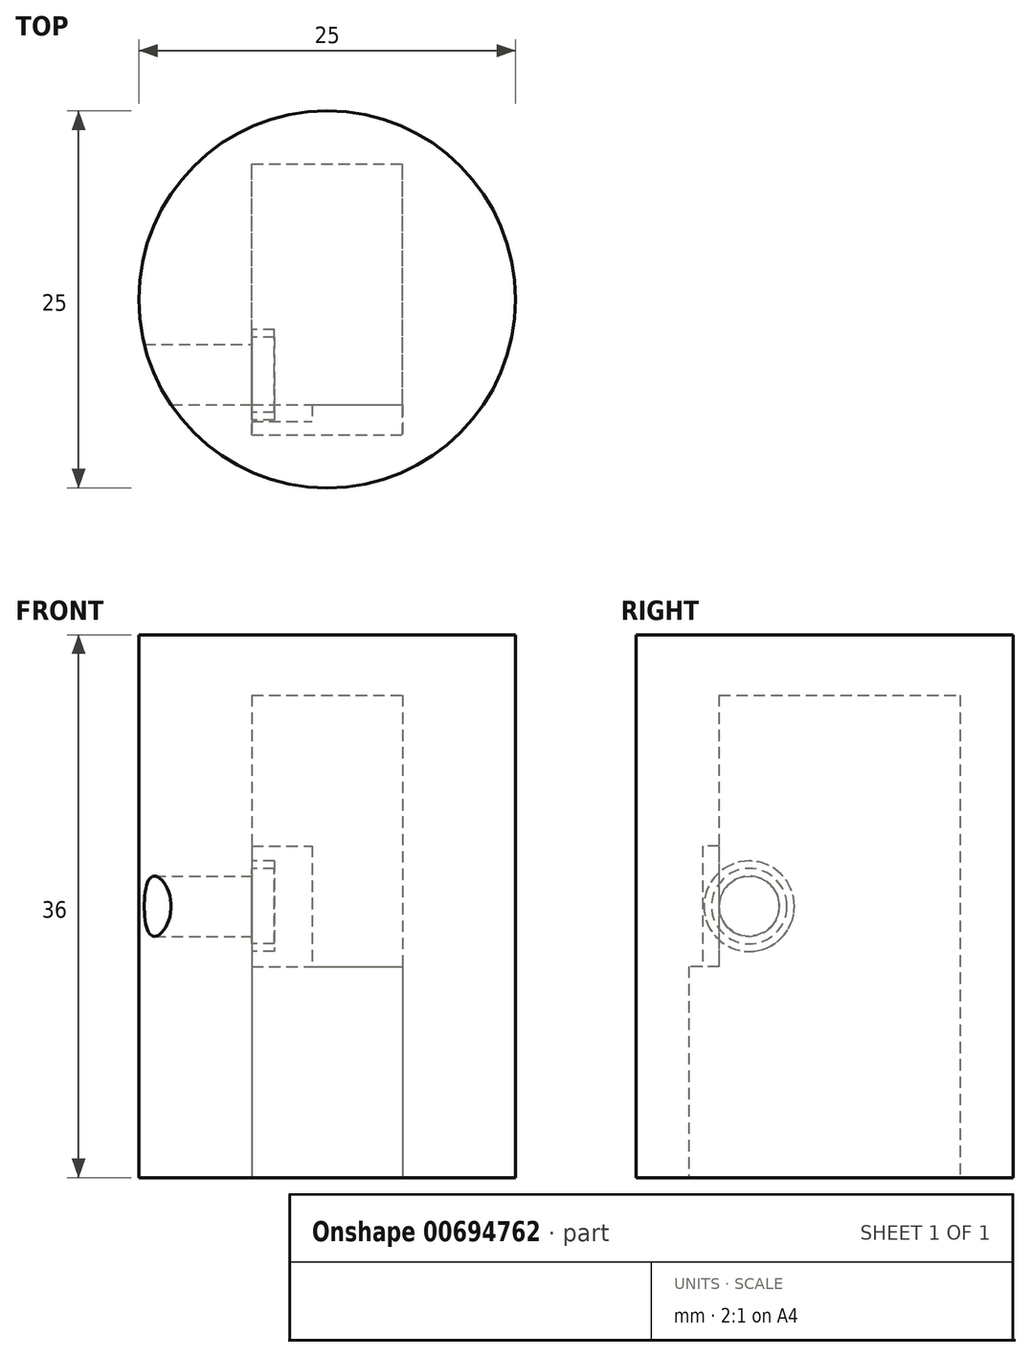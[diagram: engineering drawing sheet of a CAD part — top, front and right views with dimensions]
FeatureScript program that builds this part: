
annotation { "Feature Type Name" : "Feature", "Feature Type Description" : "" }
export const myFeature = defineFeature(function(context is Context, id is Id, definition is map)
    precondition{}
    {
        {
            var Q0;
            Q0=qCreatedBy(makeId("Top.planeOp"),FACE);
            var sketch = newSketch(context, id + "F0", { "sketchPlane" : qUnion([Q0])});
            skCircle(sketch, "E0", {"center": v(0, 0) * mm, "radius": 12.5 * mm});
            skSolve(sketch);
        }
        {
            var Q0;
            Q0 = qSketchRegion(id + "F0", true);
            extrude(context, id + "F1", {"entities" : qUnion([Q0]), "depth" : 36 * mm, "offsetDistance" : 25 * mm});
        }
        {
            var Q0;
            Q0=makeQuery(id+"F1.opExtrude","CAP_FACE",FACE,{"disambiguationData":[OSD([sQuery(id+"F0.wireOp",EDGE,"E0")])],"isStart":true});
            var sketch = newSketch(context, id + "F2", { "sketchPlane" : qUnion([Q0])});
            skLineSegment(sketch, "E1.bottom", {"start": v(-5, 7) * mm, "end": v(5, 7) * mm});
            skLineSegment(sketch, "E1.top", {"start": v(-5, -9) * mm, "end": v(5, -9) * mm});
            skLineSegment(sketch, "E1.left", {"start": v(-5, 7) * mm, "end": v(-5, -9) * mm});
            skLineSegment(sketch, "E1.right", {"start": v(5, 7) * mm, "end": v(5, -9) * mm});
            skSolve(sketch);
        }
        {
            var Q0;
            Q0=makeQuery(id+"F2.imprint","IMPRINT",FACE,{"disambiguationData":[TD([[makeQuery(id+"F2.imprint","IMPRINT",EDGE,{"derivedFrom":sQuery(id+"F2.wireOp",EDGE,"E1.bottom")}),-1.0]])]});
            extrude(context, id + "F3", {"entities" : qUnion([Q0]), "operationType" : NewBodyOperationType.REMOVE, "oppositeDirection" : true, "depth" : 32 * mm, "offsetDistance" : 25 * mm});
        }
        {
            var Q0;
            Q0=makeQuery(id+"F1.opExtrude","CAP_FACE",FACE,{"disambiguationData":[OSD([sQuery(id+"F0.wireOp",EDGE,"E0")])],"isStart":true});
            var sketch = newSketch(context, id + "F4", { "sketchPlane" : qUnion([Q0])});
            skLineSegment(sketch, "E2.left", {"start": v(-5, 7) * mm, "end": v(-5, 7) * mm});
            skLineSegment(sketch, "E2.right", {"start": v(5, 7) * mm, "end": v(5, 7) * mm});
            skLineSegment(sketch, "E3.bottom", {"start": v(-5, 7) * mm, "end": v(5, 7) * mm});
            skLineSegment(sketch, "E3.top", {"start": v(-5, 9) * mm, "end": v(5, 9) * mm});
            skLineSegment(sketch, "E3.left", {"start": v(-5, 7) * mm, "end": v(-5, 9) * mm});
            skLineSegment(sketch, "E3.right", {"start": v(5, 7) * mm, "end": v(5, 9) * mm});
            skSolve(sketch);
        }
        {
            var Q0;
            Q0 = qSketchRegion(id + "F4", true);
            extrude(context, id + "F5", {"entities" : qUnion([Q0]), "operationType" : NewBodyOperationType.REMOVE, "oppositeDirection" : true, "depth" : 14 * mm, "offsetDistance" : 25 * mm});
        }
        {
            var Q0;
            Q0=makeQuery(id+"F5.boolean.opBoolean","MERGE",FACE,{"derivedFrom":[makeQuery(id+"F3.boolean.opBoolean","COPY",FACE,{"derivedFrom":makeQuery(id+"F3.opExtrude","SWEPT_FACE",FACE,{"disambiguationData":[OSD([sQuery(id+"F2.wireOp",EDGE,"E1.left")])]})}),makeQuery(id+"F5.opExtrude","SWEPT_FACE",FACE,{"disambiguationData":[OSD([sQuery(id+"F4.wireOp",EDGE,"E3.left")])]})]});
            var sketch = newSketch(context, id + "F6", { "sketchPlane" : qUnion([Q0])});
            skLineSegment(sketch, "E4", {"start": v(-5, 32) * mm, "end": v(-5, 0) * mm, "construction": true});
            skLineSegment(sketch, "E5", {"start": v(-9, 18) * mm, "end": v(9, 18) * mm, "construction": true});
            skPoint(sketch, "E6", {"position": v(-5, 18) * mm});
            skSolve(sketch);
        }
        {
            var Q0;
            Q0=sQuery(id+"F6.wireOp",VERTEX,"E6");
            var Q1;
            Q1=makeQuery(id+"F1.opExtrude","SWEPT_BODY",BODY,{"disambiguationData":[OSD([sQuery(id+"F0.wireOp",EDGE,"E0")])]});
            hole(context, id + "F7", {"style" : HoleStyle.SIMPLE, "endStyle" : HoleEndStyle.THROUGH, "holeDiameter" : 4 * mm, "majorDiameter" : 5 * mm, "isTappedThrough" : true, "tappedDepth" : 12 * mm, "tapClearance" : 3, "locations" : qUnion([Q0]), "scope" : qUnion([Q1])});
        }
        {
            var Q0;
            Q0=makeQuery(id+"F5.boolean.opBoolean","MERGE",FACE,{"derivedFrom":[makeQuery(id+"F3.boolean.opBoolean","COPY",FACE,{"derivedFrom":makeQuery(id+"F3.opExtrude","SWEPT_FACE",FACE,{"disambiguationData":[OSD([sQuery(id+"F2.wireOp",EDGE,"E1.left")])]})}),makeQuery(id+"F5.opExtrude","SWEPT_FACE",FACE,{"disambiguationData":[OSD([sQuery(id+"F4.wireOp",EDGE,"E3.left")])]})]});
            var sketch = newSketch(context, id + "F8", { "sketchPlane" : qUnion([Q0])});
            skCircle(sketch, "E7", {"center": v(-5, 18) * mm, "radius": 3 * mm});
            skCircle(sketch, "E8", {"center": v(-5, 18) * mm, "radius": 2.5 * mm});
            skPoint(sketch, "E9.top.start.orphan", {"position": v(-7.5, 22) * mm});
            skPoint(sketch, "E10.orphan", {"position": v(-2.5, 22) * mm});
            skPoint(sketch, "E9.bottom.start.orphan", {"position": v(-7.5, 14) * mm});
            skSolve(sketch);
        }
        {
            var Q0;
            Q0=makeQuery(id+"F5.boolean.opBoolean","COPY",FACE,{"derivedFrom":makeQuery(id+"F5.opExtrude","CAP_FACE",FACE,{"disambiguationData":[OSD([sQuery(id+"F4.wireOp",EDGE,"E3.bottom"),sQuery(id+"F4.wireOp",EDGE,"E3.top"),sQuery(id+"F4.wireOp",EDGE,"E3.left"),sQuery(id+"F4.wireOp",EDGE,"E3.right")])],"isStart":false})});
            var sketch = newSketch(context, id + "F9", { "sketchPlane" : qUnion([Q0])});
            skLineSegment(sketch, "E11.bottom", {"start": v(-5, 7) * mm, "end": v(-1, 7) * mm});
            skLineSegment(sketch, "E11.top", {"start": v(-5, 8.1) * mm, "end": v(-1, 8.1) * mm});
            skLineSegment(sketch, "E11.left", {"start": v(-5, 7) * mm, "end": v(-5, 8.1) * mm});
            skLineSegment(sketch, "E11.right", {"start": v(-1, 7) * mm, "end": v(-1, 8.1) * mm});
            skSolve(sketch);
        }
        {
            var Q0;
            Q0=makeQuery(id+"F9.imprint","IMPRINT",FACE,{"disambiguationData":[TD([[makeQuery(id+"F9.imprint","IMPRINT",EDGE,{"derivedFrom":sQuery(id+"F9.wireOp",EDGE,"E11.bottom")}),1.0]])]});
            extrude(context, id + "F10", {"entities" : qUnion([Q0]), "operationType" : NewBodyOperationType.REMOVE, "oppositeDirection" : true, "depth" : 8 * mm, "offsetDistance" : 25 * mm});
        }
        {
            var Q0;
            Q0 = qSketchRegion(id + "F8", true);
            extrude(context, id + "F11", {"entities" : qUnion([Q0]), "operationType" : NewBodyOperationType.ADD, "depth" : 1.5 * mm, "offsetDistance" : 25 * mm});
        }
    });
